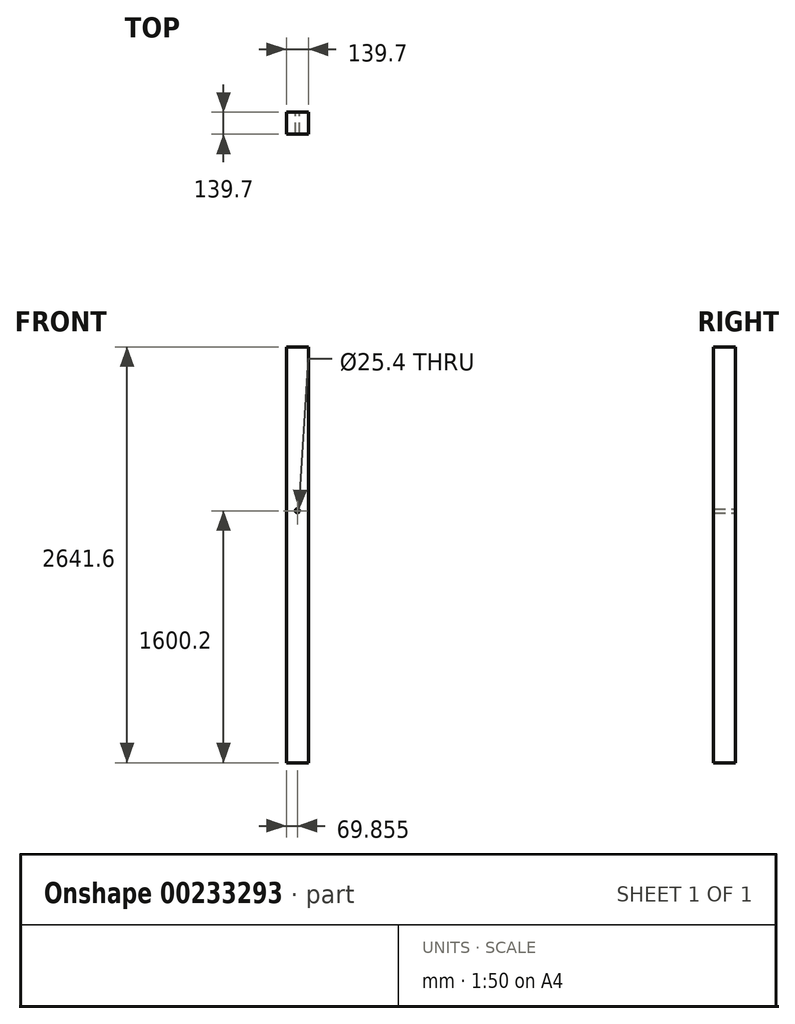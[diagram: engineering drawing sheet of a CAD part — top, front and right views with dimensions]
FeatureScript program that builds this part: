
annotation { "Feature Type Name" : "Feature", "Feature Type Description" : "" }
export const myFeature = defineFeature(function(context is Context, id is Id, definition is map)
    precondition{}
    {
        {
            var Q0;
            Q0=qCreatedBy(makeId("Front.planeOp"),FACE);
            var sketch = newSketch(context, id + "F0", { "sketchPlane" : qUnion([Q0])});
            skLineSegment(sketch, "E0.bottom", {"start": v(-68.28, 2513.61) * mm, "end": v(71.42, 2513.61) * mm});
            skLineSegment(sketch, "E0.top", {"start": v(-68.28, -127.99) * mm, "end": v(71.42, -127.99) * mm});
            skLineSegment(sketch, "E0.left", {"start": v(-68.28, 2513.61) * mm, "end": v(-68.28, -127.99) * mm});
            skLineSegment(sketch, "E0.right", {"start": v(71.42, 2513.61) * mm, "end": v(71.42, -127.99) * mm});
            skCircle(sketch, "E1", {"center": v(1.57, 1472.21) * mm, "radius": 12.7 * mm});
            skSolve(sketch);
        }
        {
            var Q0;
            Q0 = qSketchRegion(id + "F0", true);
            extrude(context, id + "F1", {"entities" : qUnion([Q0]), "depth" : 139.7 * mm});
        }
    });
